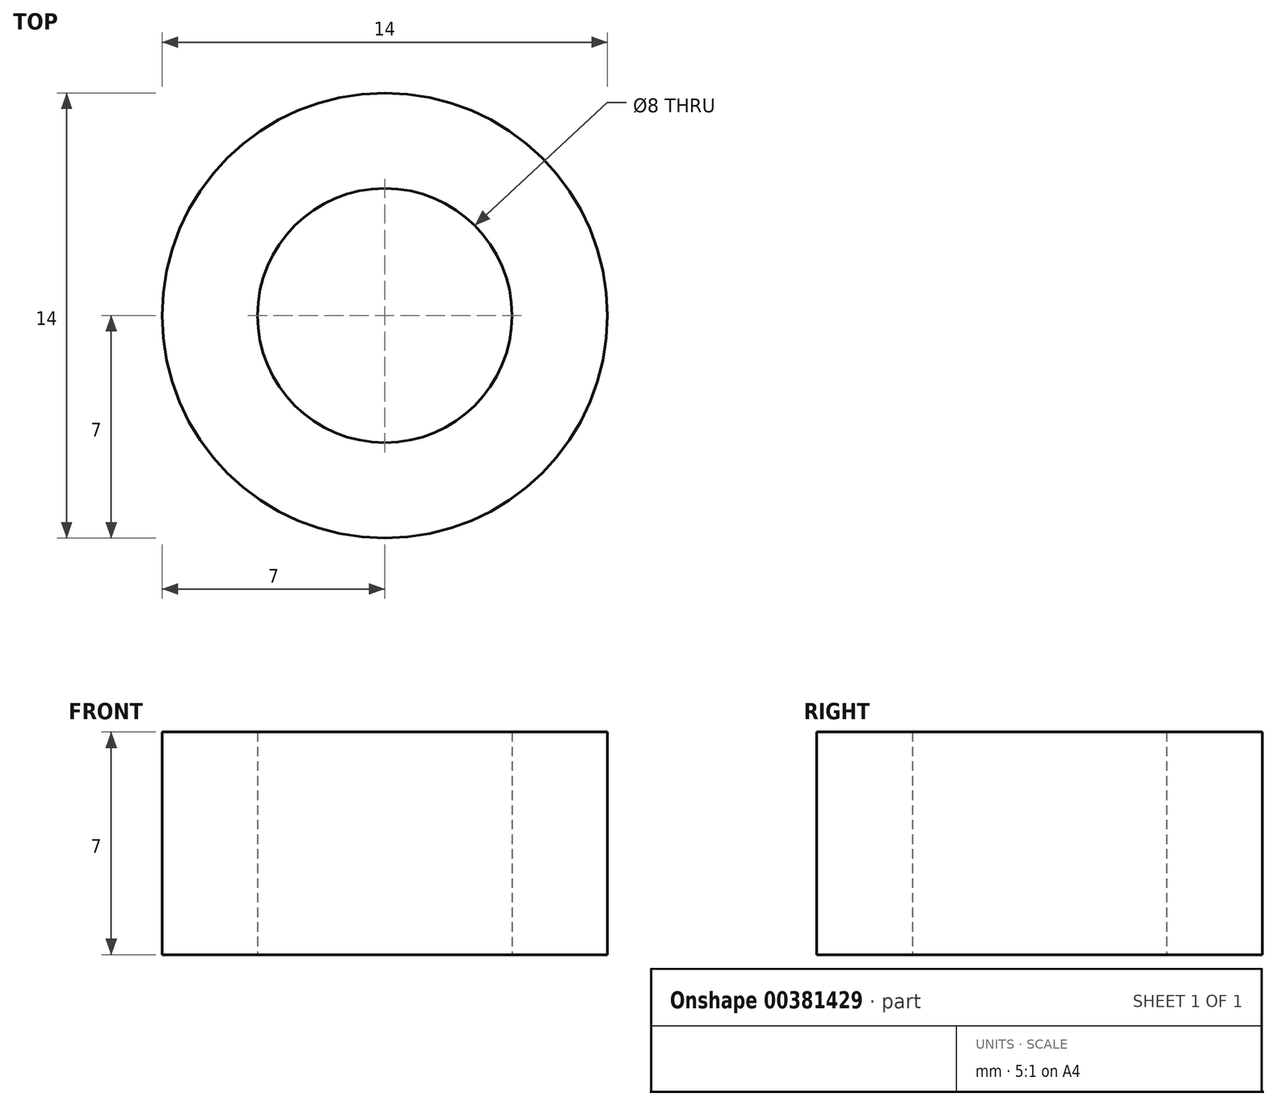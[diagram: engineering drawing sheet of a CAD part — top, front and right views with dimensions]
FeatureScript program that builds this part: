
annotation { "Feature Type Name" : "Feature", "Feature Type Description" : "" }
export const myFeature = defineFeature(function(context is Context, id is Id, definition is map)
    precondition{}
    {
        {
            var Q0;
            Q0=qCreatedBy(makeId("Top.planeOp"),FACE);
            var sketch = newSketch(context, id + "F0", { "sketchPlane" : qUnion([Q0])});
            skCircle(sketch, "E0", {"center": v(0, 0) * mm, "radius": 7 * mm});
            skCircle(sketch, "E1", {"center": v(0, 0) * mm, "radius": 4 * mm});
            skSolve(sketch);
        }
        {
            var Q0;
            Q0 = qSketchRegion(id + "F0", true);
            extrude(context, id + "F1", {"entities" : qUnion([Q0]), "depth" : 7 * mm});
        }
    });
